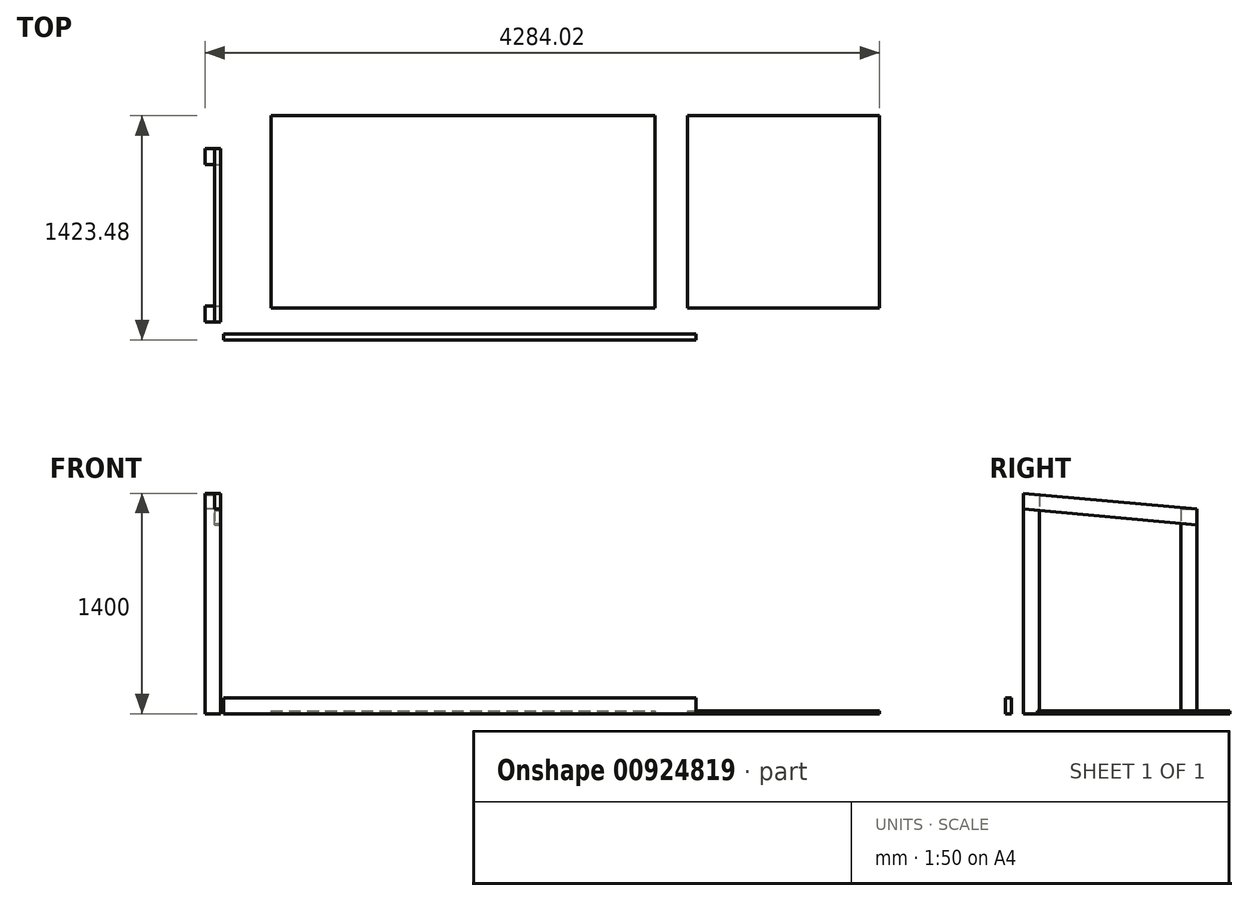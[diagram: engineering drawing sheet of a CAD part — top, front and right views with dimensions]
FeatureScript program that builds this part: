
annotation { "Feature Type Name" : "Feature", "Feature Type Description" : "" }
export const myFeature = defineFeature(function(context is Context, id is Id, definition is map)
    precondition{}
    {
        {
            var Q0;
            Q0=qCreatedBy(makeId("Top.planeOp"),FACE);
            var sketch = newSketch(context, id + "F0", { "sketchPlane" : qUnion([Q0])});
            skLineSegment(sketch, "E0.bottom", {"start": v(-18.37, 0) * mm, "end": v(-118.37, 0) * mm});
            skLineSegment(sketch, "E0.top", {"start": v(-18.37, 100) * mm, "end": v(-118.37, 100) * mm});
            skLineSegment(sketch, "E0.left", {"start": v(-18.37, 0) * mm, "end": v(-18.37, 100) * mm});
            skLineSegment(sketch, "E0.right", {"start": v(-118.37, 0) * mm, "end": v(-118.37, 100) * mm});
            skLineSegment(sketch, "E1.bottom", {"start": v(48.74, 0) * mm, "end": v(148.74, 0) * mm});
            skLineSegment(sketch, "E1.top", {"start": v(48.74, 100) * mm, "end": v(148.74, 100) * mm});
            skLineSegment(sketch, "E1.left", {"start": v(48.74, 0) * mm, "end": v(48.74, 100) * mm});
            skLineSegment(sketch, "E1.right", {"start": v(148.74, 0) * mm, "end": v(148.74, 100) * mm});
            skLineSegment(sketch, "E2.bottom", {"start": v(-18.37, 1000) * mm, "end": v(-118.37, 1000) * mm});
            skLineSegment(sketch, "E2.top", {"start": v(-18.37, 1100) * mm, "end": v(-118.37, 1100) * mm});
            skLineSegment(sketch, "E2.left", {"start": v(-18.37, 1000) * mm, "end": v(-18.37, 1100) * mm});
            skLineSegment(sketch, "E2.right", {"start": v(-118.37, 1000) * mm, "end": v(-118.37, 1100) * mm});
            skSolve(sketch);
        }
        {
            var Q0;
            Q0=makeQuery(id+"F0.imprint","IMPRINT",FACE,{"disambiguationData":[TD([[makeQuery(id+"F0.imprint","IMPRINT",EDGE,{"derivedFrom":sQuery(id+"F0.wireOp",EDGE,"E0.bottom")}),-1.0]])]});
            extrude(context, id + "F1", {"entities" : qUnion([Q0]), "depth" : 1400 * mm, "offsetDistance" : 25 * mm});
        }
        {
            var Q0;
            Q0=makeQuery(id+"F0.imprint","IMPRINT",FACE,{"disambiguationData":[TD([[makeQuery(id+"F0.imprint","IMPRINT",EDGE,{"derivedFrom":sQuery(id+"F0.wireOp",EDGE,"E2.bottom")}),-1.0]])]});
            extrude(context, id + "F2", {"entities" : qUnion([Q0]), "depth" : 1300 * mm, "offsetDistance" : 25 * mm});
        }
        {
            var Q0;
            Q0=qCreatedBy(makeId("Right.planeOp"),FACE);
            var sketch = newSketch(context, id + "F3", { "sketchPlane" : qUnion([Q0])});
            skLineSegment(sketch, "E3.bottom", {"start": v(-114.09, 0) * mm, "end": v(-76.09, 0) * mm});
            skLineSegment(sketch, "E3.top", {"start": v(-114.09, 100) * mm, "end": v(-76.09, 100) * mm});
            skLineSegment(sketch, "E3.left", {"start": v(-114.09, 0) * mm, "end": v(-114.09, 100) * mm});
            skLineSegment(sketch, "E3.right", {"start": v(-76.09, 0) * mm, "end": v(-76.09, 100) * mm});
            skLineSegment(sketch, "E4.bottom", {"start": v(-187.41, 0) * mm, "end": v(-225.41, 0) * mm});
            skLineSegment(sketch, "E4.top", {"start": v(-187.41, 100) * mm, "end": v(-225.41, 100) * mm});
            skLineSegment(sketch, "E4.left", {"start": v(-187.41, 0) * mm, "end": v(-187.41, 100) * mm});
            skLineSegment(sketch, "E4.right", {"start": v(-225.41, 0) * mm, "end": v(-225.41, 100) * mm});
            skSolve(sketch);
        }
        {
            var Q0;
            Q0=makeQuery(id+"F3.imprint","IMPRINT",FACE,{"disambiguationData":[TD([[makeQuery(id+"F3.imprint","IMPRINT",EDGE,{"derivedFrom":sQuery(id+"F3.wireOp",EDGE,"E3.bottom")}),1.0]])]});
            extrude(context, id + "F4", {"entities" : qUnion([Q0]), "depth" : 3000 * mm, "offsetDistance" : 25 * mm});
        }
        {
            var Q0;
            Q0=qCreatedBy(makeId("Top.planeOp"),FACE);
            var sketch = newSketch(context, id + "F5", { "sketchPlane" : qUnion([Q0])});
            skLineSegment(sketch, "E5.bottom", {"start": v(300.07, 89.39) * mm, "end": v(2740.07, 89.39) * mm});
            skLineSegment(sketch, "E5.top", {"start": v(300.07, 1309.39) * mm, "end": v(2740.07, 1309.39) * mm});
            skLineSegment(sketch, "E5.left", {"start": v(300.07, 89.39) * mm, "end": v(300.07, 1309.39) * mm});
            skLineSegment(sketch, "E5.right", {"start": v(2740.07, 89.39) * mm, "end": v(2740.07, 1309.39) * mm});
            skLineSegment(sketch, "E6.bottom", {"start": v(2945.65, 89.39) * mm, "end": v(4165.65, 89.39) * mm});
            skLineSegment(sketch, "E6.top", {"start": v(2945.65, 1309.39) * mm, "end": v(4165.65, 1309.39) * mm});
            skLineSegment(sketch, "E6.left", {"start": v(2945.65, 89.39) * mm, "end": v(2945.65, 1309.39) * mm});
            skLineSegment(sketch, "E6.right", {"start": v(4165.65, 89.39) * mm, "end": v(4165.65, 1309.39) * mm});
            skSolve(sketch);
        }
        {
            var Q0;
            Q0=makeQuery(id+"F5.imprint","IMPRINT",FACE,{"disambiguationData":[TD([[makeQuery(id+"F5.imprint","IMPRINT",EDGE,{"derivedFrom":sQuery(id+"F5.wireOp",EDGE,"E5.bottom")}),1.0]])]});
            var Q1;
            Q1=makeQuery(id+"F5.imprint","IMPRINT",FACE,{"disambiguationData":[TD([[makeQuery(id+"F5.imprint","IMPRINT",EDGE,{"derivedFrom":sQuery(id+"F5.wireOp",EDGE,"E6.bottom")}),1.0]])]});
            extrude(context, id + "F6", {"entities" : qUnion([Q0, Q1]), "depth" : 18 * mm, "offsetDistance" : 25 * mm});
        }
        {
            var Q0;
            Q0=makeQuery(id+"F1.opExtrude","SWEPT_FACE",FACE,{"disambiguationData":[OSD([sQuery(id+"F0.wireOp",EDGE,"E0.left")])]});
            var sketch = newSketch(context, id + "F7", { "sketchPlane" : qUnion([Q0])});
            skLineSegment(sketch, "E7.0.0", {"start": v(1000, 0) * mm, "end": v(1100, 0) * mm});
            skLineSegment(sketch, "E7.0.1", {"start": v(1100, 0) * mm, "end": v(1100, 1300) * mm});
            skLineSegment(sketch, "E7.0.2", {"start": v(1100, 1300) * mm, "end": v(1000, 1300) * mm});
            skLineSegment(sketch, "E7.0.3", {"start": v(1000, 1300) * mm, "end": v(1000, 0) * mm});
            skLineSegment(sketch, "E8", {"start": v(0, 1400) * mm, "end": v(1100, 1300) * mm});
            skLineSegment(sketch, "E9", {"start": v(0, 1299.59) * mm, "end": v(1100, 1199.59) * mm});
            skLineSegment(sketch, "E10", {"start": v(1000, 1300) * mm, "end": v(1000, 1309.1) * mm});
            skSolve(sketch);
        }
        {
            var Q0;
            {var subQ1=sQuery(id+"F0.wireOp",EDGE,"E0.left");var subQ2=makeQuery(id+"F1.opExtrude","CAP_EDGE",EDGE,{"disambiguationData":[OSD([subQ1])],"isStart":false});Q0=makeQuery(id+"F7.imprint","IMPRINT",FACE,{"disambiguationData":[TD([[makeQuery(id+"F7.imprint","IMPRINT",EDGE,{"derivedFrom":subQ2}),-1.0]])]});}
            extrude(context, id + "F8", {"entities" : qUnion([Q0]), "operationType" : NewBodyOperationType.REMOVE, "endBound" : BoundingType.UP_TO_NEXT, "oppositeDirection" : true, "depth" : 25 * mm, "offsetDistance" : 25 * mm});
        }
        {
            var Q0;
            {var subQ0=sQuery(id+"F7.wireOp",EDGE,"cRVhyxke-61BW-YOns-RdtK-qVUDOrJTacq0");Q0=makeQuery(id+"F7.imprint","IMPRINT",FACE,{"disambiguationData":[TD([[makeQuery(id+"F7.imprint","IMPRINT",EDGE,{"derivedFrom":subQ0}),1.0]])]});}
            var Q1;
            {var subQ1=sQuery(id+"F0.wireOp",EDGE,"E0.left");var subQ2=makeQuery(id+"F1.opExtrude","SWEPT_EDGE",EDGE,{"disambiguationData":[OSD([sQuery(id+"F0.wireOp",EDGE,"E0.bottom"),subQ1])]});var subQ6=sQuery(id+"F7.wireOp",EDGE,"E9");var subQ7=makeQuery(id+"F7.imprint","INTERSECT",VERTEX,{"derivedFrom":[subQ2,subQ6]});Q1=makeQuery(id+"F7.imprint","IMPRINT",FACE,{"disambiguationData":[TD([[makeQuery(id+"F7.imprint","IMPRINT",EDGE,{"disambiguationData":[TD([[subQ7,-1.0]])],"derivedFrom":subQ6}),1.0]])]});}
            var Q2;
            {var subQ0=sQuery(id+"F7.wireOp",EDGE,"E7.0.2");Q2=makeQuery(id+"F7.imprint","IMPRINT",FACE,{"disambiguationData":[TD([[makeQuery(id+"F7.imprint","IMPRINT",EDGE,{"derivedFrom":subQ0}),1.0]])]});}
            extrude(context, id + "F9", {"entities" : qUnion([Q0, Q1, Q2]), "operationType" : NewBodyOperationType.REMOVE, "oppositeDirection" : true, "depth" : 40 * mm, "offsetDistance" : 25 * mm});
        }
        {
            var Q0;
            {var subQ1=sQuery(id+"F0.wireOp",EDGE,"E0.left");var subQ2=makeQuery(id+"F1.opExtrude","SWEPT_EDGE",EDGE,{"disambiguationData":[OSD([sQuery(id+"F0.wireOp",EDGE,"E0.bottom"),subQ1])]});var subQ6=sQuery(id+"F7.wireOp",EDGE,"E9");var subQ7=makeQuery(id+"F7.imprint","INTERSECT",VERTEX,{"derivedFrom":[subQ2,subQ6]});Q0=makeQuery(id+"F7.imprint","IMPRINT",FACE,{"disambiguationData":[TD([[makeQuery(id+"F7.imprint","IMPRINT",EDGE,{"disambiguationData":[TD([[subQ7,-1.0]])],"derivedFrom":subQ6}),1.0]])]});}
            var Q1;
            {var subQ1=sQuery(id+"F7.wireOp",EDGE,"E7.0.2");Q1=makeQuery(id+"F7.imprint","IMPRINT",FACE,{"disambiguationData":[TD([[makeQuery(id+"F7.imprint","IMPRINT",EDGE,{"derivedFrom":subQ1}),-1.0]])]});}
            var Q2;
            {var subQ0=sQuery(id+"F7.wireOp",EDGE,"E7.0.2");Q2=makeQuery(id+"F7.imprint","IMPRINT",FACE,{"disambiguationData":[TD([[makeQuery(id+"F7.imprint","IMPRINT",EDGE,{"derivedFrom":subQ0}),1.0]])]});}
            var Q3;
            {var subQ5=sQuery(id+"F7.wireOp",EDGE,"E10");Q3=makeQuery(id+"F7.imprint","IMPRINT",FACE,{"disambiguationData":[TD([[makeQuery(id+"F7.imprint","IMPRINT",EDGE,{"derivedFrom":subQ5}),1.0]])]});}
            extrude(context, id + "F10", {"entities" : qUnion([Q0, Q1, Q2, Q3]), "oppositeDirection" : true, "depth" : 38 * mm, "offsetDistance" : 25 * mm});
        }
    });
